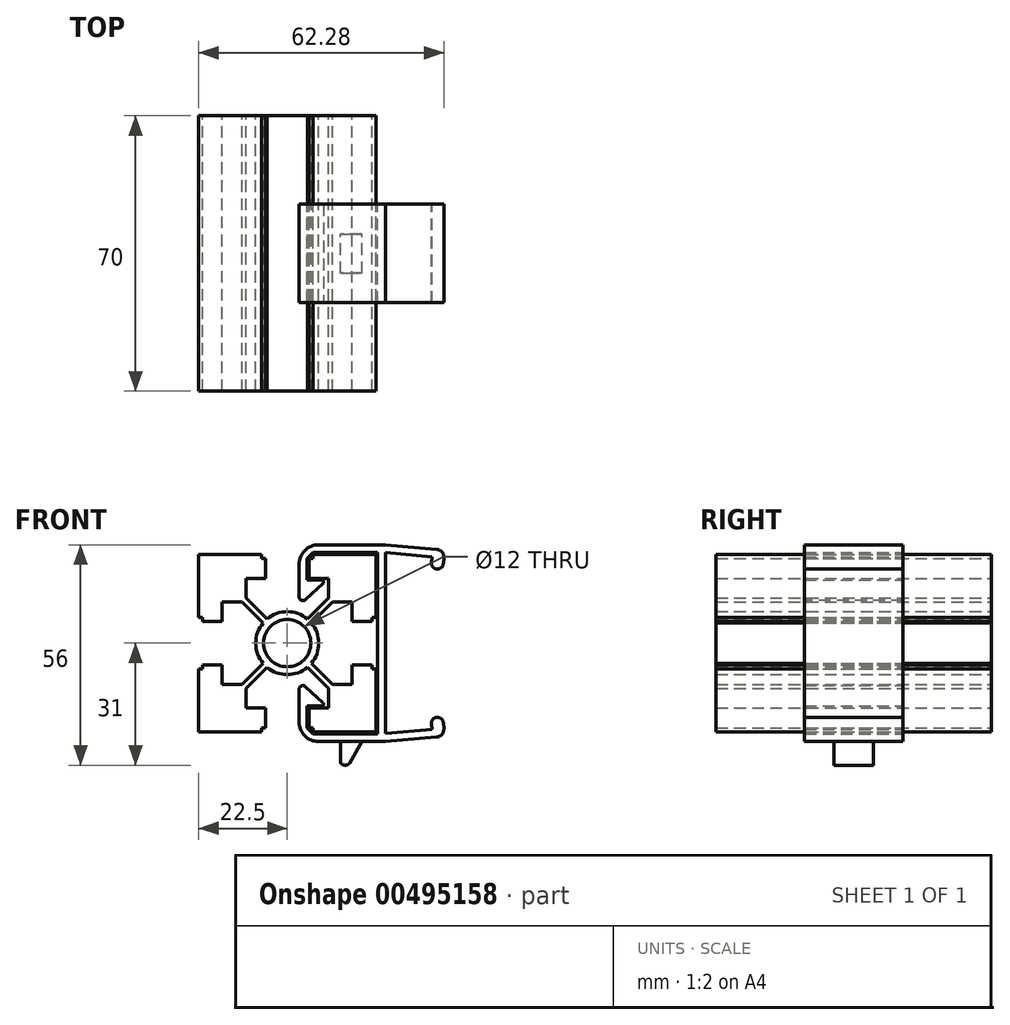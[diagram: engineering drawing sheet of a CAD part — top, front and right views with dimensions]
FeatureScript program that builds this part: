
annotation { "Feature Type Name" : "Feature", "Feature Type Description" : "" }
export const myFeature = defineFeature(function(context is Context, id is Id, definition is map)
    precondition{}
    {
        {
            var Q0;
            Q0=qCreatedBy(makeId("Front.planeOp"),FACE);
            var sketch = newSketch(context, id + "F0", { "sketchPlane" : qUnion([Q0])});
            skPoint(sketch, "E0.middle", {"position": v(0, 0) * mm});
            skPoint(sketch, "E1", {"position": v(-6.5, 22.5) * mm});
            skLineSegment(sketch, "E2", {"start": v(-6.5, 22.5) * mm, "end": v(-6.5, 21.5) * mm});
            skLineSegment(sketch, "E3", {"start": v(-6.5, 21.5) * mm, "end": v(-5.5, 21.5) * mm});
            skLineSegment(sketch, "E4", {"start": v(-5.5, 21.5) * mm, "end": v(-5.5, 16.5) * mm});
            skLineSegment(sketch, "E5", {"start": v(-5.5, 16.5) * mm, "end": v(-10.5, 16.5) * mm});
            skLineSegment(sketch, "E6", {"start": v(-10.5, 16.5) * mm, "end": v(-10.5, 11.5) * mm});
            skCircle(sketch, "E7", {"center": v(0, 0) * mm, "radius": 8 * mm});
            skLineSegment(sketch, "E8", {"start": v(-22.5, 22.5) * mm, "end": v(-6.5, 22.5) * mm});
            skLineSegment(sketch, "E9", {"start": v(22.5, 22.5) * mm, "end": v(6.5, 22.5) * mm});
            skLineSegment(sketch, "E10", {"start": v(6.5, 22.5) * mm, "end": v(6.5, 21.5) * mm});
            skLineSegment(sketch, "E11", {"start": v(6.5, 21.5) * mm, "end": v(5.5, 21.5) * mm});
            skLineSegment(sketch, "E12", {"start": v(5.5, 21.5) * mm, "end": v(5.5, 16.5) * mm});
            skLineSegment(sketch, "E13", {"start": v(5.5, 16.5) * mm, "end": v(10.5, 16.5) * mm});
            skLineSegment(sketch, "E14", {"start": v(10.5, 16.5) * mm, "end": v(10.5, 11.5) * mm});
            skPoint(sketch, "E15", {"position": v(-22.5, 6.5) * mm});
            skLineSegment(sketch, "E16", {"start": v(-22.5, 6.5) * mm, "end": v(-22.5, 22.5) * mm});
            skLineSegment(sketch, "E17", {"start": v(-22.5, 6.5) * mm, "end": v(-21.5, 6.5) * mm});
            skLineSegment(sketch, "E18", {"start": v(-21.5, 6.5) * mm, "end": v(-21.5, 5.5) * mm});
            skLineSegment(sketch, "E19", {"start": v(-21.5, 5.5) * mm, "end": v(-16.5, 5.5) * mm});
            skLineSegment(sketch, "E20", {"start": v(-16.5, 5.5) * mm, "end": v(-16.5, 10.5) * mm});
            skLineSegment(sketch, "E21", {"start": v(-16.5, 10.5) * mm, "end": v(-11.5, 10.5) * mm});
            skLineSegment(sketch, "E22", {"start": v(-22.5, -22.5) * mm, "end": v(-22.5, -6.5) * mm});
            skLineSegment(sketch, "E23", {"start": v(-22.5, -6.5) * mm, "end": v(-21.5, -6.5) * mm});
            skLineSegment(sketch, "E24", {"start": v(-21.5, -6.5) * mm, "end": v(-21.5, -5.5) * mm});
            skLineSegment(sketch, "E25", {"start": v(-21.5, -5.5) * mm, "end": v(-16.5, -5.5) * mm});
            skLineSegment(sketch, "E26", {"start": v(-16.5, -5.5) * mm, "end": v(-16.5, -10.5) * mm});
            skLineSegment(sketch, "E27", {"start": v(-16.5, -10.5) * mm, "end": v(-11.5, -10.5) * mm});
            skLineSegment(sketch, "E28", {"start": v(-22.5, -22.5) * mm, "end": v(-6.5, -22.5) * mm});
            skLineSegment(sketch, "E29", {"start": v(-6.5, -22.5) * mm, "end": v(-6.5, -21.5) * mm});
            skLineSegment(sketch, "E30", {"start": v(-6.5, -21.5) * mm, "end": v(-5.5, -21.5) * mm});
            skLineSegment(sketch, "E31", {"start": v(-5.5, -21.5) * mm, "end": v(-5.5, -16.5) * mm});
            skLineSegment(sketch, "E32", {"start": v(-5.5, -16.5) * mm, "end": v(-10.5, -16.5) * mm});
            skLineSegment(sketch, "E33", {"start": v(-10.5, -16.5) * mm, "end": v(-10.5, -11.5) * mm});
            skLineSegment(sketch, "E34", {"start": v(22.5, -22.5) * mm, "end": v(6.5, -22.5) * mm});
            skLineSegment(sketch, "E35", {"start": v(6.5, -22.5) * mm, "end": v(6.5, -21.5) * mm});
            skLineSegment(sketch, "E36", {"start": v(6.5, -21.5) * mm, "end": v(5.5, -21.5) * mm});
            skLineSegment(sketch, "E37", {"start": v(5.5, -21.5) * mm, "end": v(5.5, -16.5) * mm});
            skLineSegment(sketch, "E38", {"start": v(5.5, -16.5) * mm, "end": v(10.5, -16.5) * mm});
            skLineSegment(sketch, "E39", {"start": v(10.5, -16.5) * mm, "end": v(10.5, -11.5) * mm});
            skLineSegment(sketch, "E40", {"start": v(22.5, -22.5) * mm, "end": v(22.5, -6.5) * mm});
            skLineSegment(sketch, "E41", {"start": v(22.5, -6.5) * mm, "end": v(21.5, -6.5) * mm});
            skLineSegment(sketch, "E42", {"start": v(21.5, -6.5) * mm, "end": v(21.5, -5.5) * mm});
            skLineSegment(sketch, "E43", {"start": v(21.5, -5.5) * mm, "end": v(16.5, -5.5) * mm});
            skLineSegment(sketch, "E44", {"start": v(16.5, -5.5) * mm, "end": v(16.5, -10.5) * mm});
            skLineSegment(sketch, "E45", {"start": v(16.5, -10.5) * mm, "end": v(11.5, -10.5) * mm});
            skLineSegment(sketch, "E46", {"start": v(22.5, 22.5) * mm, "end": v(22.5, 6.5) * mm});
            skLineSegment(sketch, "E47", {"start": v(22.5, 6.5) * mm, "end": v(21.5, 6.5) * mm});
            skLineSegment(sketch, "E48", {"start": v(21.5, 6.5) * mm, "end": v(21.5, 5.5) * mm});
            skLineSegment(sketch, "E49", {"start": v(21.5, 5.5) * mm, "end": v(16.5, 5.5) * mm});
            skLineSegment(sketch, "E50", {"start": v(16.5, 5.5) * mm, "end": v(16.5, 10.5) * mm});
            skLineSegment(sketch, "E51", {"start": v(16.5, 10.5) * mm, "end": v(11.5, 10.5) * mm});
            skPoint(sketch, "E52", {"position": v(-5.13, 6.13) * mm});
            skPoint(sketch, "E53", {"position": v(-6.13, 5.13) * mm});
            skPoint(sketch, "E54", {"position": v(5.13, -6.13) * mm});
            skPoint(sketch, "E55", {"position": v(6.13, -5.13) * mm});
            skPoint(sketch, "E56", {"position": v(5.13, 6.13) * mm});
            skPoint(sketch, "E57", {"position": v(6.13, 5.13) * mm});
            skPoint(sketch, "E58", {"position": v(-6.13, -5.13) * mm});
            skPoint(sketch, "E59", {"position": v(-5.13, -6.13) * mm});
            skLineSegment(sketch, "E60", {"start": v(-10.5, 11.5) * mm, "end": v(-5.13, 6.13) * mm});
            skLineSegment(sketch, "E61", {"start": v(-11.5, 10.5) * mm, "end": v(-6.13, 5.13) * mm});
            skLineSegment(sketch, "E62", {"start": v(5.13, 6.13) * mm, "end": v(10.5, 11.5) * mm});
            skLineSegment(sketch, "E63", {"start": v(6.13, 5.13) * mm, "end": v(11.5, 10.5) * mm});
            skLineSegment(sketch, "E64", {"start": v(6.13, -5.13) * mm, "end": v(11.5, -10.5) * mm});
            skLineSegment(sketch, "E65", {"start": v(5.13, -6.13) * mm, "end": v(10.5, -11.5) * mm});
            skLineSegment(sketch, "E66", {"start": v(-5.13, -6.13) * mm, "end": v(-10.5, -11.5) * mm});
            skLineSegment(sketch, "E67", {"start": v(-11.5, -10.5) * mm, "end": v(-6.13, -5.13) * mm});
            skCircle(sketch, "E68", {"center": v(0, 0) * mm, "radius": 6 * mm});
            skSolve(sketch);
        }
        {
            var Q0;
            Q0=qSketchRegion(id+"F0",true);
            extrude(context, id + "F1", {"entities" : qUnion([Q0]), "endBound" : BoundingType.SYMMETRIC, "depth" : 70 * mm});
        }
        {
            var Q0;
            Q0=qCreatedBy(makeId("Front.planeOp"),FACE);
            var sketch = newSketch(context, id + "F2", { "sketchPlane" : qUnion([Q0])});
            skPoint(sketch, "E69", {"position": v(5.5, 21.5) * mm});
            skLineSegment(sketch, "E70", {"start": v(5.5, 16.5) * mm, "end": v(5.5, 16) * mm, "construction": true});
            skPoint(sketch, "E71", {"position": v(6.5, 22.5) * mm});
            skPoint(sketch, "E72", {"position": v(22.5, 22.5) * mm});
            skPoint(sketch, "E73", {"position": v(22.5, 6.5) * mm});
            skLineSegment(sketch, "E74", {"start": v(22.5, 22.5) * mm, "end": v(22.5, 23) * mm, "construction": true});
            skLineSegment(sketch, "E75", {"start": v(22.5, 22.5) * mm, "end": v(23, 22.5) * mm, "construction": true});
            skLineSegment(sketch, "E76", {"start": v(22.5, 6.5) * mm, "end": v(23, 6.5) * mm, "construction": true});
            skLineSegment(sketch, "E77", {"start": v(6.5, 22.5) * mm, "end": v(6.5, 23) * mm, "construction": true});
            skLineSegment(sketch, "E78", {"start": v(5.5, 16.5) * mm, "end": v(5, 16.5) * mm, "construction": true});
            skLineSegment(sketch, "E79", {"start": v(5.5, 21.5) * mm, "end": v(5, 21.5) * mm, "construction": true});
            skLineSegment(sketch, "E80", {"start": v(5, 21.5) * mm, "end": v(6.5, 23) * mm});
            skPoint(sketch, "E81", {"position": v(23, 23) * mm});
            skLineSegment(sketch, "E82", {"start": v(23, 23) * mm, "end": v(6.5, 23) * mm});
            skLineSegment(sketch, "E83", {"start": v(23, 23) * mm, "end": v(22.5, 22.5) * mm, "construction": true});
            skLineSegment(sketch, "E84", {"start": v(5, 21.5) * mm, "end": v(3, 21.5) * mm, "construction": true});
            skLineSegment(sketch, "E85", {"start": v(5, 16.5) * mm, "end": v(3, 16.5) * mm, "construction": true});
            skLineSegment(sketch, "E86", {"start": v(3, 21.5) * mm, "end": v(3, 9.5) * mm});
            skLineSegment(sketch, "E87", {"start": v(6.5, 23) * mm, "end": v(6.5, 25) * mm, "construction": true});
            skLineSegment(sketch, "E88", {"start": v(22.5, 23) * mm, "end": v(22.5, 25) * mm, "construction": true});
            skLineSegment(sketch, "E89", {"start": v(23, 22.5) * mm, "end": v(25, 22.5) * mm, "construction": true});
            skLineSegment(sketch, "E90", {"start": v(23, 6.5) * mm, "end": v(25, 6.5) * mm, "construction": true});
            skLineSegment(sketch, "E91", {"start": v(25, 22.5) * mm, "end": v(25, 0) * mm});
            skLineSegment(sketch, "E92", {"start": v(22.5, 25) * mm, "end": v(6.5, 25) * mm});
            skLineSegment(sketch, "E93", {"start": v(23, 23) * mm, "end": v(25, 25) * mm, "construction": true});
            skLineSegment(sketch, "E94", {"start": v(22.5, 25) * mm, "end": v(25, 25) * mm});
            skLineSegment(sketch, "E95", {"start": v(25, 22.5) * mm, "end": v(25, 25) * mm});
            skLineSegment(sketch, "E96", {"start": v(3, 21.5) * mm, "end": v(3, 25) * mm});
            skLineSegment(sketch, "E97", {"start": v(3, 25) * mm, "end": v(6.5, 25) * mm});
            skPoint(sketch, "E98", {"position": v(6.5, 21.5) * mm});
            skLineSegment(sketch, "E99", {"start": v(3, 25) * mm, "end": v(6.5, 21.5) * mm, "construction": true});
            skLineSegment(sketch, "E100", {"start": v(23, 23) * mm, "end": v(23, 0) * mm});
            skLineSegment(sketch, "E101", {"start": v(0, 0) * mm, "end": v(40.87, 0) * mm, "construction": true});
            skLineSegment(sketch, "E102", {"start": v(5.5, 16.5) * mm, "end": v(5, 16) * mm, "construction": true});
            skLineSegment(sketch, "E103", {"start": v(5, 21.5) * mm, "end": v(5, 16) * mm});
            skLineSegment(sketch, "E104", {"start": v(5, 16) * mm, "end": v(10, 16) * mm});
            skLineSegment(sketch, "E105", {"start": v(3, 9.5) * mm, "end": v(10, 16) * mm});
            skLineSegment(sketch, "E106.MirrorCS", {"start": v(23, -23) * mm, "end": v(22.5, -22.5) * mm, "construction": true});
            skLineSegment(sketch, "E107.MirrorCS", {"start": v(5.5, -21.5) * mm, "end": v(5, -21.5) * mm, "construction": true});
            skLineSegment(sketch, "E108.MirrorCS", {"start": v(22.5, -22.5) * mm, "end": v(23, -22.5) * mm, "construction": true});
            skLineSegment(sketch, "E109.MirrorCS", {"start": v(22.5, -22.5) * mm, "end": v(22.5, -23) * mm, "construction": true});
            skLineSegment(sketch, "E110.MirrorCS", {"start": v(5.5, -16.5) * mm, "end": v(5, -16) * mm, "construction": true});
            skLineSegment(sketch, "E111.MirrorCS", {"start": v(5.5, -16.5) * mm, "end": v(5.5, -16) * mm, "construction": true});
            skLineSegment(sketch, "E112.MirrorCS", {"start": v(5.5, -16.5) * mm, "end": v(5, -16.5) * mm, "construction": true});
            skLineSegment(sketch, "E113.MirrorCS", {"start": v(6.5, -22.5) * mm, "end": v(6.5, -23) * mm, "construction": true});
            skLineSegment(sketch, "E114.MirrorCS", {"start": v(22.5, -6.5) * mm, "end": v(23, -6.5) * mm, "construction": true});
            skLineSegment(sketch, "E115.MirrorCS", {"start": v(5, -21.5) * mm, "end": v(6.5, -23) * mm});
            skLineSegment(sketch, "E116.MirrorCS", {"start": v(23, -23) * mm, "end": v(6.5, -23) * mm});
            skLineSegment(sketch, "E117.MirrorCS", {"start": v(6.5, -23) * mm, "end": v(6.5, -25) * mm, "construction": true});
            skLineSegment(sketch, "E118.MirrorCS", {"start": v(3, -25) * mm, "end": v(6.5, -21.5) * mm, "construction": true});
            skLineSegment(sketch, "E119.MirrorCS", {"start": v(5, -21.5) * mm, "end": v(5, -16) * mm});
            skLineSegment(sketch, "E120.MirrorCS", {"start": v(23, -6.5) * mm, "end": v(25, -6.5) * mm, "construction": true});
            skLineSegment(sketch, "E121.MirrorCS", {"start": v(22.5, -23) * mm, "end": v(22.5, -25) * mm, "construction": true});
            skPoint(sketch, "E122.MirrorP", {"position": v(23, -23) * mm});
            skLineSegment(sketch, "E123.MirrorCS", {"start": v(25, -22.5) * mm, "end": v(25, -25) * mm});
            skLineSegment(sketch, "E124.MirrorCS", {"start": v(3, -9.5) * mm, "end": v(10, -16) * mm});
            skPoint(sketch, "E125.MirrorP", {"position": v(22.5, -22.5) * mm});
            skLineSegment(sketch, "E126.MirrorCS", {"start": v(3, -25) * mm, "end": v(6.5, -25) * mm});
            skLineSegment(sketch, "E127.MirrorCS", {"start": v(3, -21.5) * mm, "end": v(3, -9.5) * mm});
            skLineSegment(sketch, "E128.MirrorCS", {"start": v(3, -21.5) * mm, "end": v(3, -25) * mm});
            skPoint(sketch, "E129.MirrorP", {"position": v(6.5, -22.5) * mm});
            skLineSegment(sketch, "E130.MirrorCS", {"start": v(23, -22.5) * mm, "end": v(25, -22.5) * mm, "construction": true});
            skPoint(sketch, "E131.MirrorP", {"position": v(5.5, -21.5) * mm});
            skPoint(sketch, "E132.MirrorP", {"position": v(6.5, -21.5) * mm});
            skLineSegment(sketch, "E133.MirrorCS", {"start": v(5, -16) * mm, "end": v(10, -16) * mm});
            skLineSegment(sketch, "E134.MirrorCS", {"start": v(5, -16.5) * mm, "end": v(3, -16.5) * mm, "construction": true});
            skLineSegment(sketch, "E135.MirrorCS", {"start": v(5, -21.5) * mm, "end": v(3, -21.5) * mm, "construction": true});
            skLineSegment(sketch, "E136.MirrorCS", {"start": v(23, -23) * mm, "end": v(25, -25) * mm, "construction": true});
            skPoint(sketch, "E137.MirrorP", {"position": v(22.5, -6.5) * mm});
            skLineSegment(sketch, "E138.MirrorCS", {"start": v(22.5, -25) * mm, "end": v(6.5, -25) * mm});
            skLineSegment(sketch, "E139.MirrorCS", {"start": v(22.5, -25) * mm, "end": v(25, -25) * mm});
            skLineSegment(sketch, "E140.MirrorCS", {"start": v(23, -23) * mm, "end": v(23, 0) * mm});
            skLineSegment(sketch, "E141.MirrorCS", {"start": v(25, -22.5) * mm, "end": v(25, 0) * mm});
            skPoint(sketch, "E142", {"position": v(14.5, 25) * mm});
            skLineSegment(sketch, "E143", {"start": v(14.5, 25) * mm, "end": v(15.5, 25) * mm});
            skLineSegment(sketch, "E144", {"start": v(14.5, 25) * mm, "end": v(13.5, 25) * mm});
            skLineSegment(sketch, "E145", {"start": v(13.5, 25) * mm, "end": v(13.5, 31) * mm});
            skLineSegment(sketch, "E146", {"start": v(13.5, 31) * mm, "end": v(15.5, 31) * mm});
            skLineSegment(sketch, "E147", {"start": v(15.5, 31) * mm, "end": v(18.96, 25) * mm});
            skLineSegment(sketch, "E148.MirrorCS", {"start": v(13.5, -25) * mm, "end": v(13.5, -31) * mm});
            skLineSegment(sketch, "E149.MirrorCS", {"start": v(13.5, -31) * mm, "end": v(15.5, -31) * mm});
            skLineSegment(sketch, "E150.MirrorCS", {"start": v(15.5, -31) * mm, "end": v(18.96, -25) * mm});
            skLineSegment(sketch, "E151", {"start": v(25, 25) * mm, "end": v(39.94, 23.7) * mm});
            skLineSegment(sketch, "E152", {"start": v(39.94, 23.7) * mm, "end": v(39.77, 21.7) * mm});
            skLineSegment(sketch, "E153", {"start": v(39.77, 21.7) * mm, "end": v(25, 23) * mm});
            skLineSegment(sketch, "E154", {"start": v(39.77, 21.7) * mm, "end": v(39.5, 18.71) * mm});
            skLineSegment(sketch, "E155", {"start": v(39.5, 18.71) * mm, "end": v(36.52, 18.97) * mm});
            skLineSegment(sketch, "E156", {"start": v(36.52, 18.97) * mm, "end": v(36.78, 21.96) * mm});
            skLineSegment(sketch, "E157.MirrorCS", {"start": v(39.77, -21.7) * mm, "end": v(39.5, -18.71) * mm});
            skLineSegment(sketch, "E158.MirrorCS", {"start": v(39.5, -18.71) * mm, "end": v(36.52, -18.97) * mm});
            skLineSegment(sketch, "E159.MirrorCS", {"start": v(39.94, -23.7) * mm, "end": v(39.77, -21.7) * mm});
            skLineSegment(sketch, "E160.MirrorCS", {"start": v(36.52, -18.97) * mm, "end": v(36.78, -21.96) * mm});
            skLineSegment(sketch, "E161.MirrorCS", {"start": v(25, -25) * mm, "end": v(39.94, -23.7) * mm});
            skLineSegment(sketch, "E162.MirrorCS", {"start": v(39.77, -21.7) * mm, "end": v(25, -23) * mm});
            skSolve(sketch);
        }
        {
            var Q0;
            Q0=makeQuery(id+"F2.imprint","IMPRINT",FACE,{"disambiguationData":[TD([[makeQuery(id+"F2.imprint","IMPRINT",EDGE,{"derivedFrom":sQuery(id+"F2.wireOp",EDGE,"E80")}),1.0]])]});
            var Q1;
            {var subQ3=sQuery(id+"F2.wireOp",EDGE,"E151");Q1=makeQuery(id+"F2.imprint","IMPRINT",FACE,{"disambiguationData":[TD([[makeQuery(id+"F2.imprint","IMPRINT",EDGE,{"derivedFrom":subQ3}),-1.0]])]});}
            var Q2;
            {var subQ0=sQuery(id+"F2.wireOp",EDGE,"E154");Q2=makeQuery(id+"F2.imprint","IMPRINT",FACE,{"disambiguationData":[TD([[makeQuery(id+"F2.imprint","IMPRINT",EDGE,{"derivedFrom":subQ0}),-1.0]])]});}
            var Q3;
            {var subQ1=sQuery(id+"F2.wireOp",EDGE,"E159.MirrorCS");Q3=makeQuery(id+"F2.imprint","IMPRINT",FACE,{"disambiguationData":[TD([[makeQuery(id+"F2.imprint","IMPRINT",EDGE,{"derivedFrom":subQ1}),1.0]])]});}
            var Q4;
            {var subQ0=sQuery(id+"F2.wireOp",EDGE,"E157.MirrorCS");Q4=makeQuery(id+"F2.imprint","IMPRINT",FACE,{"disambiguationData":[TD([[makeQuery(id+"F2.imprint","IMPRINT",EDGE,{"derivedFrom":subQ0}),1.0]])]});}
            extrude(context, id + "F3", {"entities" : qUnion([Q0, Q1, Q2, Q3, Q4]), "endBound" : BoundingType.SYMMETRIC, "depth" : 25 * mm});
        }
        {
            var Q0;
            {var subQ0=sQuery(id+"F2.wireOp",EDGE,"E143");Q0=makeQuery(id+"F2.imprint","IMPRINT",FACE,{"disambiguationData":[TD([[makeQuery(id+"F2.imprint","IMPRINT",EDGE,{"derivedFrom":subQ0}),1.0]])]});}
            var Q1;
            {var subQ0=sQuery(id+"F2.wireOp",EDGE,"E148.MirrorCS");Q1=makeQuery(id+"F2.imprint","IMPRINT",FACE,{"disambiguationData":[TD([[makeQuery(id+"F2.imprint","IMPRINT",EDGE,{"derivedFrom":subQ0}),1.0]])]});}
            extrude(context, id + "F4", {"entities" : qUnion([Q0, Q1]), "operationType" : NewBodyOperationType.ADD, "endBound" : BoundingType.SYMMETRIC, "depth" : 10 * mm});
        }
        {
            var Q0;
            Q0=makeQuery(id+"F3.opExtrude","SWEPT_EDGE",EDGE,{"disambiguationData":[OSD([sQuery(id+"F2.wireOp",EDGE,"E96"),sQuery(id+"F2.wireOp",EDGE,"E97")])]});
            var Q1;
            Q1=makeQuery(id+"F3.opExtrude","SWEPT_EDGE",EDGE,{"disambiguationData":[OSD([sQuery(id+"F2.wireOp",EDGE,"E126.MirrorCS"),sQuery(id+"F2.wireOp",EDGE,"E128.MirrorCS")])]});
            fillet(context, id + "F5", {"entities" : qUnion([Q0, Q1]), "radius" : 5 * mm, "tangentPropagation" : true, "allowEdgeOverflow" : false});
        }
        {
            var Q0;
            Q0=makeQuery(id+"F3.opExtrude","SWEPT_EDGE",EDGE,{"disambiguationData":[OSD([sQuery(id+"F2.wireOp",EDGE,"E104"),sQuery(id+"F2.wireOp",EDGE,"E105")])]});
            var Q1;
            Q1=makeQuery(id+"F3.opExtrude","SWEPT_EDGE",EDGE,{"disambiguationData":[OSD([sQuery(id+"F2.wireOp",EDGE,"E124.MirrorCS"),sQuery(id+"F2.wireOp",EDGE,"E133.MirrorCS")])]});
            fillet(context, id + "F6", {"entities" : qUnion([Q0, Q1]), "radius" : 0.5 * mm, "tangentPropagation" : true, "allowEdgeOverflow" : false});
        }
        {
            var Q0;
            Q0=makeQuery(id+"F3.opExtrude","SWEPT_EDGE",EDGE,{"disambiguationData":[OSD([sQuery(id+"F2.wireOp",EDGE,"E86"),sQuery(id+"F2.wireOp",EDGE,"E105")])]});
            var Q1;
            Q1=makeQuery(id+"F3.opExtrude","SWEPT_EDGE",EDGE,{"disambiguationData":[OSD([sQuery(id+"F2.wireOp",EDGE,"E124.MirrorCS"),sQuery(id+"F2.wireOp",EDGE,"E127.MirrorCS")])]});
            fillet(context, id + "F7", {"entities" : qUnion([Q0, Q1]), "radius" : 1 * mm, "tangentPropagation" : true, "allowEdgeOverflow" : false});
        }
        {
            var Q0;
            Q0=makeQuery(id+"F4.opExtrude","SWEPT_EDGE",EDGE,{"disambiguationData":[OSD([sQuery(id+"F2.wireOp",EDGE,"E145"),sQuery(id+"F2.wireOp",EDGE,"E146")])]});
            var Q1;
            Q1=makeQuery(id+"F4.opExtrude","SWEPT_EDGE",EDGE,{"disambiguationData":[OSD([sQuery(id+"F2.wireOp",EDGE,"E146"),sQuery(id+"F2.wireOp",EDGE,"E147")])]});
            var Q2;
            Q2=makeQuery(id+"F4.opExtrude","SWEPT_EDGE",EDGE,{"disambiguationData":[OSD([sQuery(id+"F2.wireOp",EDGE,"E149.MirrorCS"),sQuery(id+"F2.wireOp",EDGE,"E150.MirrorCS")])]});
            var Q3;
            Q3=makeQuery(id+"F4.opExtrude","SWEPT_EDGE",EDGE,{"disambiguationData":[OSD([sQuery(id+"F2.wireOp",EDGE,"E148.MirrorCS"),sQuery(id+"F2.wireOp",EDGE,"E149.MirrorCS")])]});
            fillet(context, id + "F8", {"entities" : qUnion([Q0, Q1, Q2, Q3]), "radius" : 1 * mm, "tangentPropagation" : true, "allowEdgeOverflow" : false});
        }
        {
            var Q0;
            Q0=makeQuery(id+"F3.opExtrude","SWEPT_EDGE",EDGE,{"disambiguationData":[OSD([sQuery(id+"F2.wireOp",EDGE,"E154"),sQuery(id+"F2.wireOp",EDGE,"E155")])]});
            var Q1;
            Q1=makeQuery(id+"F3.opExtrude","SWEPT_EDGE",EDGE,{"disambiguationData":[OSD([sQuery(id+"F2.wireOp",EDGE,"E155"),sQuery(id+"F2.wireOp",EDGE,"E156")])]});
            var Q2;
            Q2=makeQuery(id+"F3.opExtrude","SWEPT_EDGE",EDGE,{"disambiguationData":[OSD([sQuery(id+"F2.wireOp",EDGE,"E157.MirrorCS"),sQuery(id+"F2.wireOp",EDGE,"E158.MirrorCS")])]});
            var Q3;
            Q3=makeQuery(id+"F3.opExtrude","SWEPT_EDGE",EDGE,{"disambiguationData":[OSD([sQuery(id+"F2.wireOp",EDGE,"E158.MirrorCS"),sQuery(id+"F2.wireOp",EDGE,"E160.MirrorCS")])]});
            fillet(context, id + "F9", {"entities" : qUnion([Q0, Q1, Q2, Q3]), "radius" : 1.5 * mm, "tangentPropagation" : true, "allowEdgeOverflow" : false});
        }
        {
            var Q0;
            Q0=makeQuery(id+"F3.opExtrude","SWEPT_EDGE",EDGE,{"disambiguationData":[OSD([sQuery(id+"F2.wireOp",EDGE,"E151"),sQuery(id+"F2.wireOp",EDGE,"E152")])]});
            var Q1;
            Q1=makeQuery(id+"F3.opExtrude","SWEPT_EDGE",EDGE,{"disambiguationData":[OSD([sQuery(id+"F2.wireOp",EDGE,"E159.MirrorCS"),sQuery(id+"F2.wireOp",EDGE,"E161.MirrorCS")])]});
            fillet(context, id + "F10", {"entities" : qUnion([Q0, Q1]), "radius" : 2 * mm, "tangentPropagation" : true, "allowEdgeOverflow" : false});
        }
    });
